# Revit family: Safety & Protection_Barrier_UltiGroup_Spanguard
name_source: partatom
category: Generic Models
revit_build: Autodesk Revit Architecture 2016 (Build: 20150220_1215(x64)
units: mm (PartAtom-declared; Revit-internal decimal feet)

## family parameters
Can host rebar = No
Cut with Voids When Loaded = No
OmniClass Number = 23.50.70.00
OmniClass Title = Loading Dock Equipment
Part Type = Normal
Room Calculation Point = No
Round Connector Dimension = Use Diameter
Shared = No

## types (2) — shared parameters
Capacity = 200 lbs
Fax = 07 846 2467
Manufacturer = UltiGroup
Send Message = http://ultigroup.co.nz
URL = www.ultigroup.co.nz
zero-valued in all types: Expected Lifespan (Years), InstallationGroup_ANZRS, Maintenance Schedule (Months), ModifiedIssue_ANZRS, Warranty Duration (Years)

## per-type parameters (varying)
| type | Description | Model |
| 18300mm Length Units | Loading Dock Removable Safety Barrier - 18300mm SpanGuard Mesh Barrier as Specified | 18300mm SpanGuard Mesh Barrier |
| 9150mm Length Units | Loading Dock Removable Safety Barrier - 9150mm SpanGuard Mesh Barrier as Specified | 9150mm SpanGuard Mesh Barrier |

## geometry (parser evidence)
native form markers: Blend x8, Sweep x3
no freeform markers — native parametric forms only
